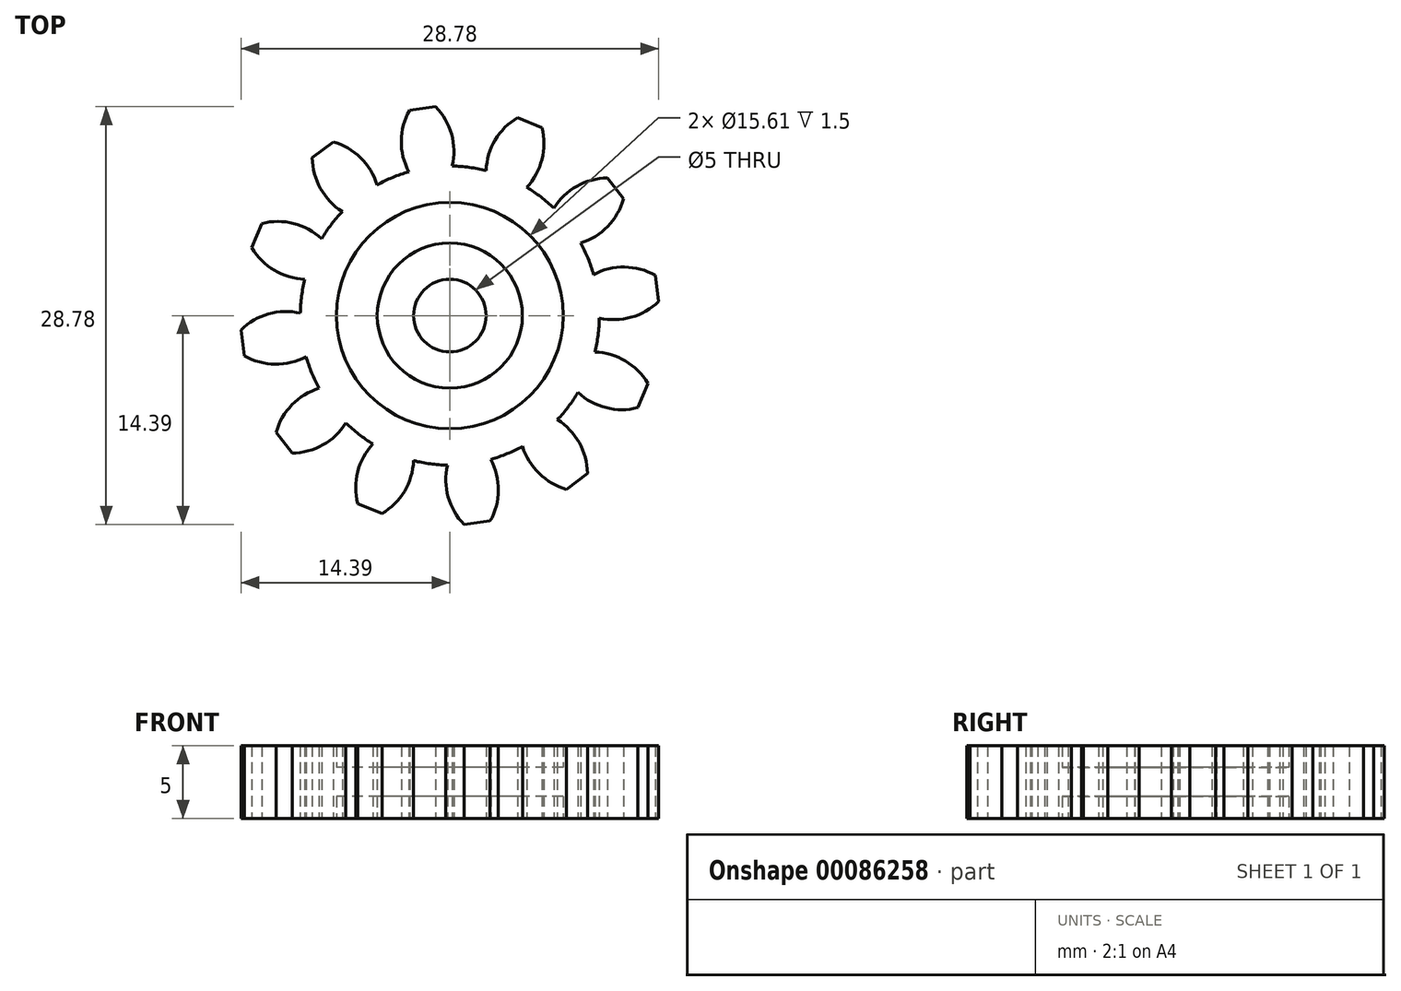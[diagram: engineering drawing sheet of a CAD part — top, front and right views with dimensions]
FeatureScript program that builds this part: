
annotation { "Feature Type Name" : "Feature", "Feature Type Description" : "" }
export const myFeature = defineFeature(function(context is Context, id is Id, definition is map)
    precondition{}
    {
        {
            assignVariable(context, id + "F0", {"name" : "Teeth", "anyValue" : 12});
        }
        {
            assignVariable(context, id + "F1", {"name" : "GearDepth", "anyValue" : 5});
        }
        {
            var Q0;
            Q0=qCreatedBy(makeId("Top.planeOp"),FACE);
            var sketch = newSketch(context, id + "F2", { "sketchPlane" : qUnion([Q0])});
            skCircle(sketch, "E0", {"center": v(0, 0) * mm, "radius": 10.3 * mm});
            skCircle(sketch, "E1", {"center": v(0, 0) * mm, "radius": 12.36 * mm, "construction": true});
            skCircle(sketch, "E2", {"center": v(0, 0) * mm, "radius": 14.43 * mm, "construction": true});
            skLineSegment(sketch, "E3", {"start": v(0, 0) * mm, "end": v(0, 17.6) * mm, "construction": true});
            skLineSegment(sketch, "E4", {"start": v(0, 0) * mm, "end": v(-2.36, 17.9) * mm, "construction": true});
            skLineSegment(sketch, "E5", {"start": v(0, 12.36) * mm, "end": v(-10.54, 12.36) * mm, "construction": true});
            skLineSegment(sketch, "E6", {"start": v(0, 12.36) * mm, "end": v(-10.3, 8.62) * mm, "construction": true});
            skCircle(sketch, "E7", {"center": v(0, 12.36) * mm, "radius": 3.1 * mm, "construction": true});
            skCircle(sketch, "E8", {"center": v(-2.9, 11.3) * mm, "radius": 3.1 * mm, "construction": true});
            skArc(sketch, "E9", {"start": v(-5.8, 12.36) * mm, "mid": v(-0.3, 9.64) * mm, "end": v(-5.08, 13.5) * mm, "construction": true});
            skArc(sketch, "E10.trimOffspring", {"start": v(0.17, 10.3) * mm, "mid": v(0.12, 12.5) * mm, "end": v(-0.98, 14.4) * mm});
            skArc(sketch, "E11.MirrorCS", {"start": v(-2.83, 9.9) * mm, "mid": v(-3.34, 12.04) * mm, "end": v(-2.78, 14.16) * mm});
            skLineSegment(sketch, "E12", {"start": v(-2.78, 14.16) * mm, "end": v(-0.98, 14.4) * mm});
            skLineSegment(sketch, "E13.19.1", {"start": v(4.07, 19.29) * mm, "end": v(4.8, 19.12) * mm});
            skCircle(sketch, "E14", {"center": v(0, 0) * mm, "radius": 2.5 * mm});
            skSolve(sketch);
        }
        {
            var Q0;
            Q0=qCreatedBy(makeId("Front.planeOp"),FACE);
            var sketch = newSketch(context, id + "F3", { "sketchPlane" : qUnion([Q0])});
            skLineSegment(sketch, "E15", {"start": v(0, 0) * mm, "end": v(0, 61.57) * mm});
            skSolve(sketch);
        }
        {
            var Q0;
            {var subQ0=sQuery(id+"F2.wireOp",EDGE,"E10.trimOffspring");Q0=makeQuery(id+"F2.imprint","IMPRINT",FACE,{"disambiguationData":[TD([[makeQuery(id+"F2.imprint","IMPRINT",EDGE,{"derivedFrom":subQ0}),1.0]])]});}
            var Q1;
            {var subQ0=sQuery(id+"F2.wireOp",EDGE,"E0");var subQ1=makeQuery(id+"F2.imprint","INTERSECT",VERTEX,{"derivedFrom":[subQ0,sQuery(id+"F2.wireOp",EDGE,"E10.trimOffspring")]});Q1=makeQuery(id+"F2.imprint","IMPRINT",FACE,{"disambiguationData":[TD([[makeQuery(id+"F2.imprint","IMPRINT",EDGE,{"disambiguationData":[TD([[subQ1,-1.0]])],"derivedFrom":subQ0}),1.0]])]});}
            var Q2;
            {var subQ0=sQuery(id+"F2.wireOp",EDGE,"E13.1.0");Q2=makeQuery(id+"F2.imprint","IMPRINT",FACE,{"disambiguationData":[TD([[makeQuery(id+"F2.imprint","IMPRINT",EDGE,{"derivedFrom":subQ0}),1.0]])]});}
            var Q3;
            {var subQ0=sQuery(id+"F2.wireOp",EDGE,"E13.2.0");Q3=makeQuery(id+"F2.imprint","IMPRINT",FACE,{"disambiguationData":[TD([[makeQuery(id+"F2.imprint","IMPRINT",EDGE,{"derivedFrom":subQ0}),1.0]])]});}
            var Q4;
            {var subQ0=sQuery(id+"F2.wireOp",EDGE,"E13.3.0");Q4=makeQuery(id+"F2.imprint","IMPRINT",FACE,{"disambiguationData":[TD([[makeQuery(id+"F2.imprint","IMPRINT",EDGE,{"derivedFrom":subQ0}),1.0]])]});}
            var Q5;
            {var subQ0=sQuery(id+"F2.wireOp",EDGE,"E13.4.0");Q5=makeQuery(id+"F2.imprint","IMPRINT",FACE,{"disambiguationData":[TD([[makeQuery(id+"F2.imprint","IMPRINT",EDGE,{"derivedFrom":subQ0}),1.0]])]});}
            var Q6;
            {var subQ0=sQuery(id+"F2.wireOp",EDGE,"E13.5.0");Q6=makeQuery(id+"F2.imprint","IMPRINT",FACE,{"disambiguationData":[TD([[makeQuery(id+"F2.imprint","IMPRINT",EDGE,{"derivedFrom":subQ0}),1.0]])]});}
            var Q7;
            {var subQ0=sQuery(id+"F2.wireOp",EDGE,"E13.6.0");Q7=makeQuery(id+"F2.imprint","IMPRINT",FACE,{"disambiguationData":[TD([[makeQuery(id+"F2.imprint","IMPRINT",EDGE,{"derivedFrom":subQ0}),1.0]])]});}
            var Q8;
            {var subQ0=sQuery(id+"F2.wireOp",EDGE,"E13.7.0");Q8=makeQuery(id+"F2.imprint","IMPRINT",FACE,{"disambiguationData":[TD([[makeQuery(id+"F2.imprint","IMPRINT",EDGE,{"derivedFrom":subQ0}),1.0]])]});}
            var Q9;
            {var subQ0=sQuery(id+"F2.wireOp",EDGE,"E13.8.0");Q9=makeQuery(id+"F2.imprint","IMPRINT",FACE,{"disambiguationData":[TD([[makeQuery(id+"F2.imprint","IMPRINT",EDGE,{"derivedFrom":subQ0}),1.0]])]});}
            var Q10;
            {var subQ0=sQuery(id+"F2.wireOp",EDGE,"E13.9.0");Q10=makeQuery(id+"F2.imprint","IMPRINT",FACE,{"disambiguationData":[TD([[makeQuery(id+"F2.imprint","IMPRINT",EDGE,{"derivedFrom":subQ0}),1.0]])]});}
            var Q11;
            {var subQ0=sQuery(id+"F2.wireOp",EDGE,"E13.10.0");Q11=makeQuery(id+"F2.imprint","IMPRINT",FACE,{"disambiguationData":[TD([[makeQuery(id+"F2.imprint","IMPRINT",EDGE,{"derivedFrom":subQ0}),1.0]])]});}
            var Q12;
            {var subQ0=sQuery(id+"F2.wireOp",EDGE,"E13.11.0");Q12=makeQuery(id+"F2.imprint","IMPRINT",FACE,{"disambiguationData":[TD([[makeQuery(id+"F2.imprint","IMPRINT",EDGE,{"derivedFrom":subQ0}),1.0]])]});}
            var Q13;
            {var subQ0=sQuery(id+"F2.wireOp",EDGE,"E13.12.0");Q13=makeQuery(id+"F2.imprint","IMPRINT",FACE,{"disambiguationData":[TD([[makeQuery(id+"F2.imprint","IMPRINT",EDGE,{"derivedFrom":subQ0}),1.0]])]});}
            var Q14;
            {var subQ0=sQuery(id+"F2.wireOp",EDGE,"E13.13.0");Q14=makeQuery(id+"F2.imprint","IMPRINT",FACE,{"disambiguationData":[TD([[makeQuery(id+"F2.imprint","IMPRINT",EDGE,{"derivedFrom":subQ0}),1.0]])]});}
            var Q15;
            {var subQ0=sQuery(id+"F2.wireOp",EDGE,"E13.14.0");Q15=makeQuery(id+"F2.imprint","IMPRINT",FACE,{"disambiguationData":[TD([[makeQuery(id+"F2.imprint","IMPRINT",EDGE,{"derivedFrom":subQ0}),1.0]])]});}
            var Q16;
            {var subQ0=sQuery(id+"F2.wireOp",EDGE,"E13.15.0");Q16=makeQuery(id+"F2.imprint","IMPRINT",FACE,{"disambiguationData":[TD([[makeQuery(id+"F2.imprint","IMPRINT",EDGE,{"derivedFrom":subQ0}),1.0]])]});}
            var Q17;
            {var subQ0=sQuery(id+"F2.wireOp",EDGE,"E13.16.0");Q17=makeQuery(id+"F2.imprint","IMPRINT",FACE,{"disambiguationData":[TD([[makeQuery(id+"F2.imprint","IMPRINT",EDGE,{"derivedFrom":subQ0}),1.0]])]});}
            var Q18;
            {var subQ0=sQuery(id+"F2.wireOp",EDGE,"E13.17.0");Q18=makeQuery(id+"F2.imprint","IMPRINT",FACE,{"disambiguationData":[TD([[makeQuery(id+"F2.imprint","IMPRINT",EDGE,{"derivedFrom":subQ0}),1.0]])]});}
            var Q19;
            {var subQ0=sQuery(id+"F2.wireOp",EDGE,"E13.18.0");Q19=makeQuery(id+"F2.imprint","IMPRINT",FACE,{"disambiguationData":[TD([[makeQuery(id+"F2.imprint","IMPRINT",EDGE,{"derivedFrom":subQ0}),1.0]])]});}
            var Q20;
            {var subQ0=sQuery(id+"F2.wireOp",EDGE,"E13.19.0");Q20=makeQuery(id+"F2.imprint","IMPRINT",FACE,{"disambiguationData":[TD([[makeQuery(id+"F2.imprint","IMPRINT",EDGE,{"derivedFrom":subQ0}),1.0]])]});}
            var Q21;
            Q21=sQuery(id+"F2.wireOp",EDGE,"E0");
            var Q22;
            Q22=sQuery(id+"F2.wireOp",EDGE,"E10.trimOffspring");
            var Q23;
            Q23=sQuery(id+"F2.wireOp",EDGE,"E12");
            var Q24;
            Q24=sQuery(id+"F2.wireOp",EDGE,"E11.MirrorCS");
            extrude(context, id + "F4", {"entities" : qUnion([Q0, Q1, Q2, Q3, Q4, Q5, Q6, Q7, Q8, Q9, Q10, Q11, Q12, Q13, Q14, Q15, Q16, Q17, Q18, Q19, Q20]), "surfaceEntities" : qUnion([Q21, Q22, Q23, Q24]), "depth" : (getVariable(context, 'GearDepth')) * mm});
        }
        {
            var Q0;
            Q0=makeQuery(id+"F4.opExtrude","SWEPT_BODY",BODY,{"disambiguationData":[OSD([sQuery(id+"F2.wireOp",EDGE,"E0"),sQuery(id+"F2.wireOp",EDGE,"E10.trimOffspring"),sQuery(id+"F2.wireOp",EDGE,"E11.MirrorCS"),sQuery(id+"F2.wireOp",EDGE,"E12"),sQuery(id+"F2.wireOp",EDGE,"E14")])]});
            var Q1;
            Q1=sQuery(id+"F3.wireOp",EDGE,"E15");
            circularPattern(context, id + "F5", {"operationType" : NewBodyOperationType.ADD, "entities" : qUnion([Q0]), "axis" : qUnion([Q1]), "angle" : (360 / getVariable(context, 'Teeth')) * degree, "instanceCount" : getVariable(context, 'Teeth')});
        }
        {
            var Q0;
            Q0=qCreatedBy(makeId("Top.planeOp"),FACE);
            var sketch = newSketch(context, id + "F6", { "sketchPlane" : qUnion([Q0])});
            skCircle(sketch, "E16", {"center": v(0, 0) * mm, "radius": 7.8 * mm});
            skCircle(sketch, "E17", {"center": v(0, 0) * mm, "radius": 5 * mm});
            skSolve(sketch);
        }
        {
            var Q0;
            Q0=makeQuery(id+"F6.imprint","IMPRINT",FACE,{"disambiguationData":[TD([[makeQuery(id+"F6.imprint","IMPRINT",EDGE,{"derivedFrom":sQuery(id+"F6.wireOp",EDGE,"E16")}),1.0]])]});
            extrude(context, id + "F7", {"entities" : qUnion([Q0]), "operationType" : NewBodyOperationType.REMOVE, "depth" : 1.5 * mm});
        }
        {
            var Q0;
            Q0=makeQuery(id+"F6.imprint","IMPRINT",FACE,{"disambiguationData":[TD([[makeQuery(id+"F6.imprint","IMPRINT",EDGE,{"derivedFrom":sQuery(id+"F6.wireOp",EDGE,"E16")}),1.0]])]});
            extrude(context, id + "F8", {"entities" : qUnion([Q0]), "operationType" : NewBodyOperationType.REMOVE, "depth" : 5 * mm, "hasSecondDirection" : true, "secondDirectionOppositeDirection" : false, "secondDirectionDepth" : 3.5 * mm});
        }
    });
